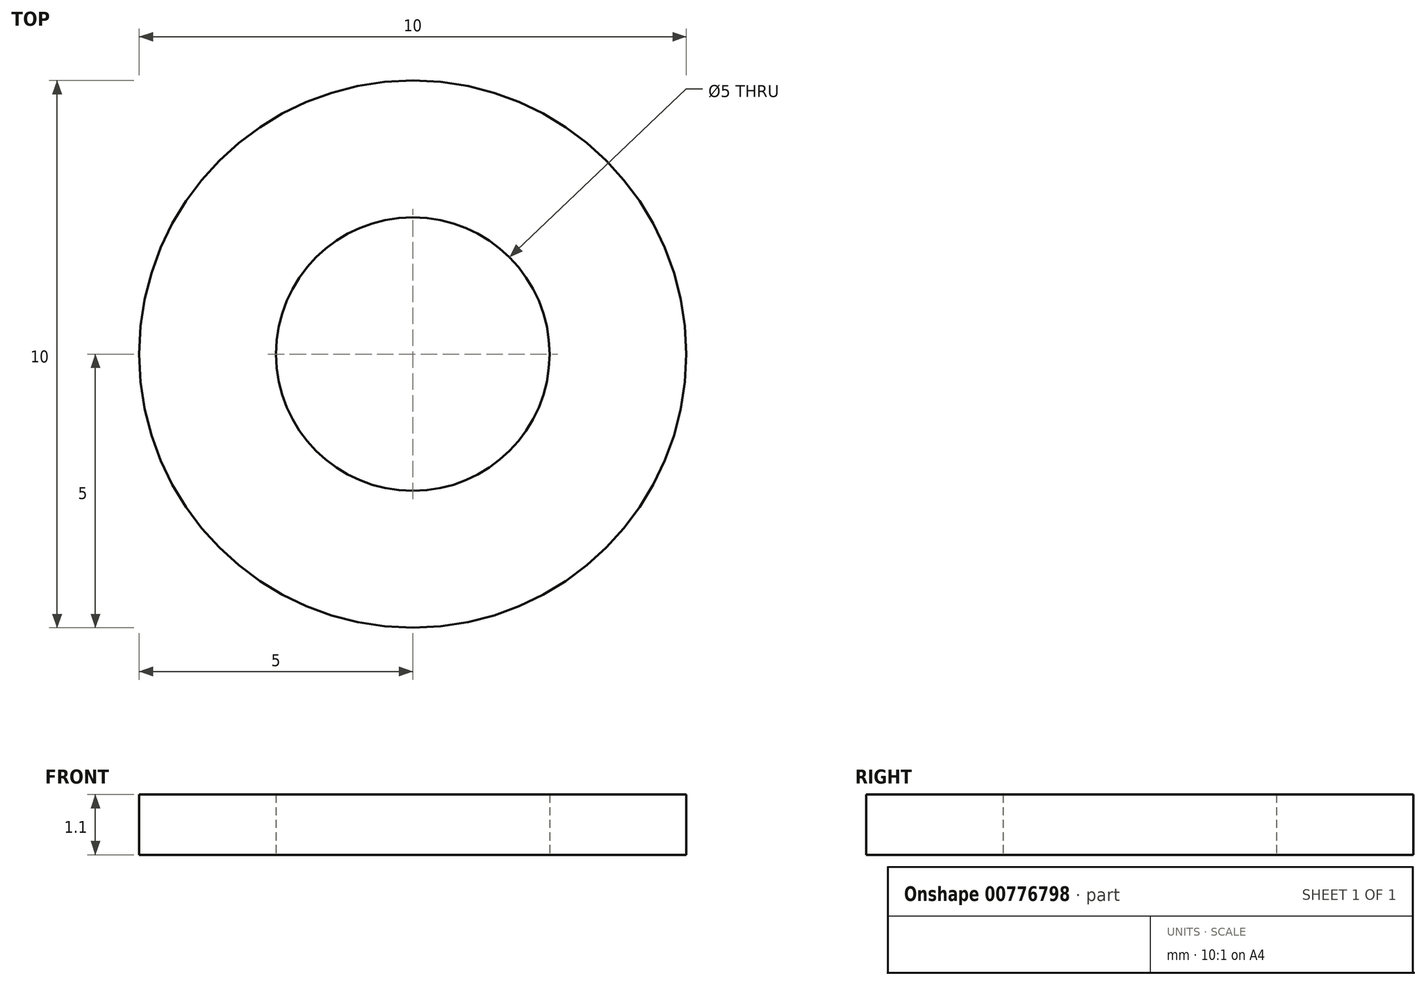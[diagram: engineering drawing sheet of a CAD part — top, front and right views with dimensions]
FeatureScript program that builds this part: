
annotation { "Feature Type Name" : "Feature", "Feature Type Description" : "" }
export const myFeature = defineFeature(function(context is Context, id is Id, definition is map)
    precondition{}
    {
        {
            var Q0;
            Q0=qCreatedBy(makeId("Top.planeOp"),FACE);
            var sketch = newSketch(context, id + "F0", { "sketchPlane" : qUnion([Q0])});
            skCircle(sketch, "E0", {"center": v(0, 0) * mm, "radius": 2.5 * mm});
            skCircle(sketch, "E1", {"center": v(0, 0) * mm, "radius": 5 * mm});
            skSolve(sketch);
        }
        {
            var Q0;
            Q0=qSketchRegion(id+"F0",true);
            var Q1;
            Q1=makeQuery(id+"F0.imprint","IMPRINT",FACE,{"disambiguationData":[TD([[makeQuery(id+"F0.imprint","IMPRINT",EDGE,{"derivedFrom":sQuery(id+"F0.wireOp",EDGE,"E0")}),-1.0]])]});
            extrude(context, id + "F1", {"entities" : qUnion([Q0, Q1]), "depth" : 1.1 * mm});
        }
    });
